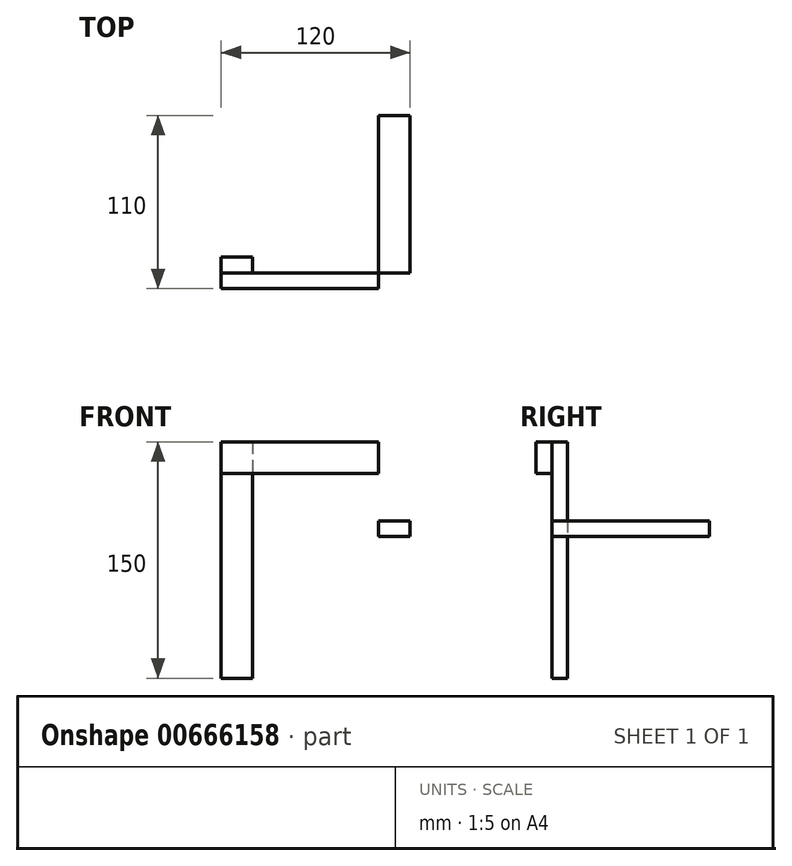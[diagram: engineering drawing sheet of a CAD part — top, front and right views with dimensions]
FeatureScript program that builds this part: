
annotation { "Feature Type Name" : "Feature", "Feature Type Description" : "" }
export const myFeature = defineFeature(function(context is Context, id is Id, definition is map)
    precondition{}
    {
        {
            var Q0;
            Q0=qCreatedBy(makeId("Top.planeOp"),FACE);
            var sketch = newSketch(context, id + "F0", { "sketchPlane" : qUnion([Q0])});
            skLineSegment(sketch, "E0.bottom", {"start": v(0, 0) * mm, "end": v(100, 0) * mm, "construction": true});
            skLineSegment(sketch, "E0.top", {"start": v(0, 100) * mm, "end": v(100, 100) * mm, "construction": true});
            skLineSegment(sketch, "E0.left", {"start": v(0, 0) * mm, "end": v(0, 100) * mm, "construction": true});
            skLineSegment(sketch, "E0.right", {"start": v(100, 0) * mm, "end": v(100, 100) * mm, "construction": true});
            skLineSegment(sketch, "E1.bottom", {"start": v(0, 0) * mm, "end": v(20, 0) * mm});
            skLineSegment(sketch, "E1.top", {"start": v(0, 10) * mm, "end": v(20, 10) * mm});
            skLineSegment(sketch, "E1.left", {"start": v(0, 0) * mm, "end": v(0, 10) * mm});
            skLineSegment(sketch, "E1.right", {"start": v(20, 0) * mm, "end": v(20, 10) * mm});
            skSolve(sketch);
        }
        {
            var Q0;
            Q0=qCreatedBy(makeId("Right.planeOp"),FACE);
            var sketch = newSketch(context, id + "F1", { "sketchPlane" : qUnion([Q0])});
            skLineSegment(sketch, "E2", {"start": v(0, 0) * mm, "end": v(0, 150) * mm, "construction": true});
            skLineSegment(sketch, "E3", {"start": v(0, 150) * mm, "end": v(100, 150) * mm, "construction": true});
            skLineSegment(sketch, "E4", {"start": v(100, 150) * mm, "end": v(100, 0) * mm, "construction": true});
            skLineSegment(sketch, "E5.bottom", {"start": v(0, 150) * mm, "end": v(-10, 150) * mm});
            skLineSegment(sketch, "E5.top", {"start": v(0, 130) * mm, "end": v(-10, 130) * mm});
            skLineSegment(sketch, "E5.left", {"start": v(0, 150) * mm, "end": v(0, 130) * mm});
            skLineSegment(sketch, "E5.right", {"start": v(-10, 150) * mm, "end": v(-10, 130) * mm});
            skSolve(sketch);
        }
        {
            var Q0;
            Q0=qCreatedBy(makeId("Front.planeOp"),FACE);
            var sketch = newSketch(context, id + "F2", { "sketchPlane" : qUnion([Q0])});
            skLineSegment(sketch, "E6", {"start": v(0, 150) * mm, "end": v(100, 100) * mm, "construction": true});
            skLineSegment(sketch, "E7", {"start": v(100, 100) * mm, "end": v(100, 0) * mm, "construction": true});
            skLineSegment(sketch, "E8.bottom", {"start": v(100, 100) * mm, "end": v(120, 100) * mm});
            skLineSegment(sketch, "E8.top", {"start": v(100, 90) * mm, "end": v(120, 90) * mm});
            skLineSegment(sketch, "E8.left", {"start": v(100, 100) * mm, "end": v(100, 90) * mm});
            skLineSegment(sketch, "E8.right", {"start": v(120, 100) * mm, "end": v(120, 90) * mm});
            skSolve(sketch);
        }
        {
            var Q0;
            Q0=makeQuery(id+"F0.imprint","IMPRINT",FACE,{"disambiguationData":[TD([[makeQuery(id+"F0.imprint","IMPRINT",EDGE,{"derivedFrom":sQuery(id+"F0.wireOp",EDGE,"E1.bottom")}),1.0]])]});
            var Q1;
            Q1=sQuery(id+"F2.wireOp",VERTEX,"E6.start");
            extrude(context, id + "F3", {"entities" : qUnion([Q0]), "endBound" : BoundingType.UP_TO_VERTEX, "depth" : 25 * mm, "endBoundEntityVertex" : qUnion([Q1]), "offsetDistance" : 25 * mm});
        }
        {
            var Q0;
            Q0=makeQuery(id+"F1.imprint","IMPRINT",FACE,{"disambiguationData":[TD([[makeQuery(id+"F1.imprint","IMPRINT",EDGE,{"derivedFrom":sQuery(id+"F1.wireOp",EDGE,"E5.bottom")}),1.0]])]});
            var Q1;
            Q1=sQuery(id+"F0.wireOp",VERTEX,"E0.right.start");
            extrude(context, id + "F4", {"entities" : qUnion([Q0]), "endBound" : BoundingType.UP_TO_VERTEX, "depth" : 25 * mm, "endBoundEntityVertex" : qUnion([Q1]), "offsetDistance" : 25 * mm});
        }
        {
            var Q0;
            Q0=makeQuery(id+"F2.imprint","IMPRINT",FACE,{"disambiguationData":[TD([[makeQuery(id+"F2.imprint","IMPRINT",EDGE,{"derivedFrom":sQuery(id+"F2.wireOp",EDGE,"E8.bottom")}),-1.0]])]});
            var Q1;
            Q1=sQuery(id+"F0.wireOp",VERTEX,"E0.right.end");
            extrude(context, id + "F5", {"entities" : qUnion([Q0]), "endBound" : BoundingType.UP_TO_VERTEX, "oppositeDirection" : true, "depth" : 25 * mm, "endBoundEntityVertex" : qUnion([Q1]), "offsetDistance" : 25 * mm});
        }
    });
